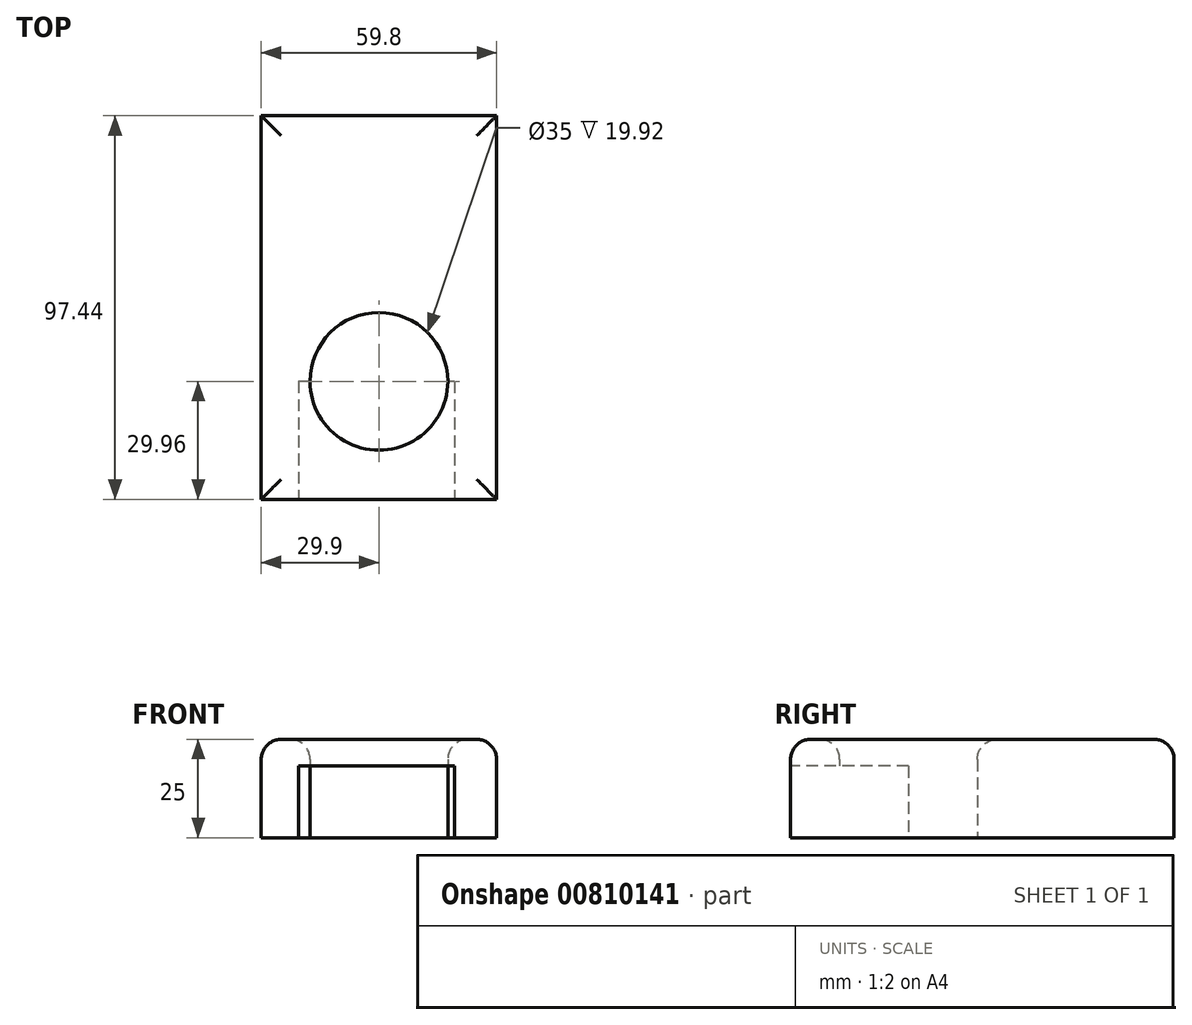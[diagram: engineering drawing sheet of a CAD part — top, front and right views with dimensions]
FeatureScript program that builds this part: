
annotation { "Feature Type Name" : "Feature", "Feature Type Description" : "" }
export const myFeature = defineFeature(function(context is Context, id is Id, definition is map)
    precondition{}
    {
        {
            var Q0;
            Q0=qCreatedBy(makeId("Top.planeOp"),FACE);
            var sketch = newSketch(context, id + "F0", { "sketchPlane" : qUnion([Q0])});
            skCircle(sketch, "E0", {"center": v(0, 0) * mm, "radius": 17.5 * mm});
            skSolve(sketch);
        }
        {
            var Q0;
            Q0=makeQuery(id+"F0.imprint","IMPRINT",FACE,{"disambiguationData":[TD([[makeQuery(id+"F0.imprint","IMPRINT",EDGE,{"derivedFrom":sQuery(id+"F0.wireOp",EDGE,"E0")}),1.0]])]});
            var sketch = newSketch(context, id + "F1", { "sketchPlane" : qUnion([Q0])});
            skLineSegment(sketch, "E1.bottom", {"start": v(29.9, -29.96) * mm, "end": v(-29.9, -29.96) * mm});
            skLineSegment(sketch, "E1.top", {"start": v(29.9, 67.48) * mm, "end": v(-29.9, 67.48) * mm});
            skLineSegment(sketch, "E1.left", {"start": v(29.9, -29.96) * mm, "end": v(29.9, 67.48) * mm});
            skLineSegment(sketch, "E1.right", {"start": v(-29.9, -29.96) * mm, "end": v(-29.9, 67.48) * mm});
            skPoint(sketch, "E1.middle", {"position": v(0, 18.76) * mm});
            skSolve(sketch);
        }
        {
            var Q0;
            Q0=makeQuery(id+"F1.imprint","IMPRINT",FACE,{"disambiguationData":[TD([[makeQuery(id+"F1.imprint","IMPRINT",EDGE,{"derivedFrom":sQuery(id+"F1.wireOp",EDGE,"E1.bottom")}),-1.0]])]});
            extrude(context, id + "F2", {"entities" : qUnion([Q0]), "depth" : 25 * mm, "offsetDistance" : 25.4 * mm});
        }
        {
            var Q0;
            Q0=makeQuery(id+"F2.opExtrude","SWEPT_FACE",FACE,{"disambiguationData":[OSD([sQuery(id+"F1.wireOp",EDGE,"E1.bottom")])]});
            var sketch = newSketch(context, id + "F3", { "sketchPlane" : qUnion([Q0])});
            skLineSegment(sketch, "E2.bottom", {"start": v(-20.38, 18.26) * mm, "end": v(19.21, 18.26) * mm});
            skLineSegment(sketch, "E2.top", {"start": v(-20.38, 0) * mm, "end": v(19.21, 0) * mm});
            skLineSegment(sketch, "E2.left", {"start": v(-20.38, 18.26) * mm, "end": v(-20.38, 0) * mm});
            skLineSegment(sketch, "E2.right", {"start": v(19.21, 18.26) * mm, "end": v(19.21, 0) * mm});
            skSolve(sketch);
        }
        {
            var Q0;
            Q0=makeQuery(id+"F3.imprint","IMPRINT",FACE,{"disambiguationData":[TD([[makeQuery(id+"F3.imprint","IMPRINT",EDGE,{"derivedFrom":sQuery(id+"F3.wireOp",EDGE,"E2.bottom")}),-1.0]])]});
            extrude(context, id + "F4", {"entities" : qUnion([Q0]), "operationType" : NewBodyOperationType.REMOVE, "oppositeDirection" : true, "depth" : 29.97 * mm, "offsetDistance" : 25.4 * mm});
        }
        {
            var Q0;
            Q0=makeQuery(id+"F2.opExtrude","CAP_FACE",FACE,{"disambiguationData":[OSD([sQuery(id+"F0.wireOp",EDGE,"E0"),sQuery(id+"F1.wireOp",EDGE,"E1.bottom"),sQuery(id+"F1.wireOp",EDGE,"E1.top"),sQuery(id+"F1.wireOp",EDGE,"E1.left"),sQuery(id+"F1.wireOp",EDGE,"E1.right")])],"isStart":false});
            fillet(context, id + "F5", {"entities" : qUnion([Q0]), "radius" : 5.08 * mm, "tangentPropagation" : true, "allowEdgeOverflow" : false});
        }
    });
